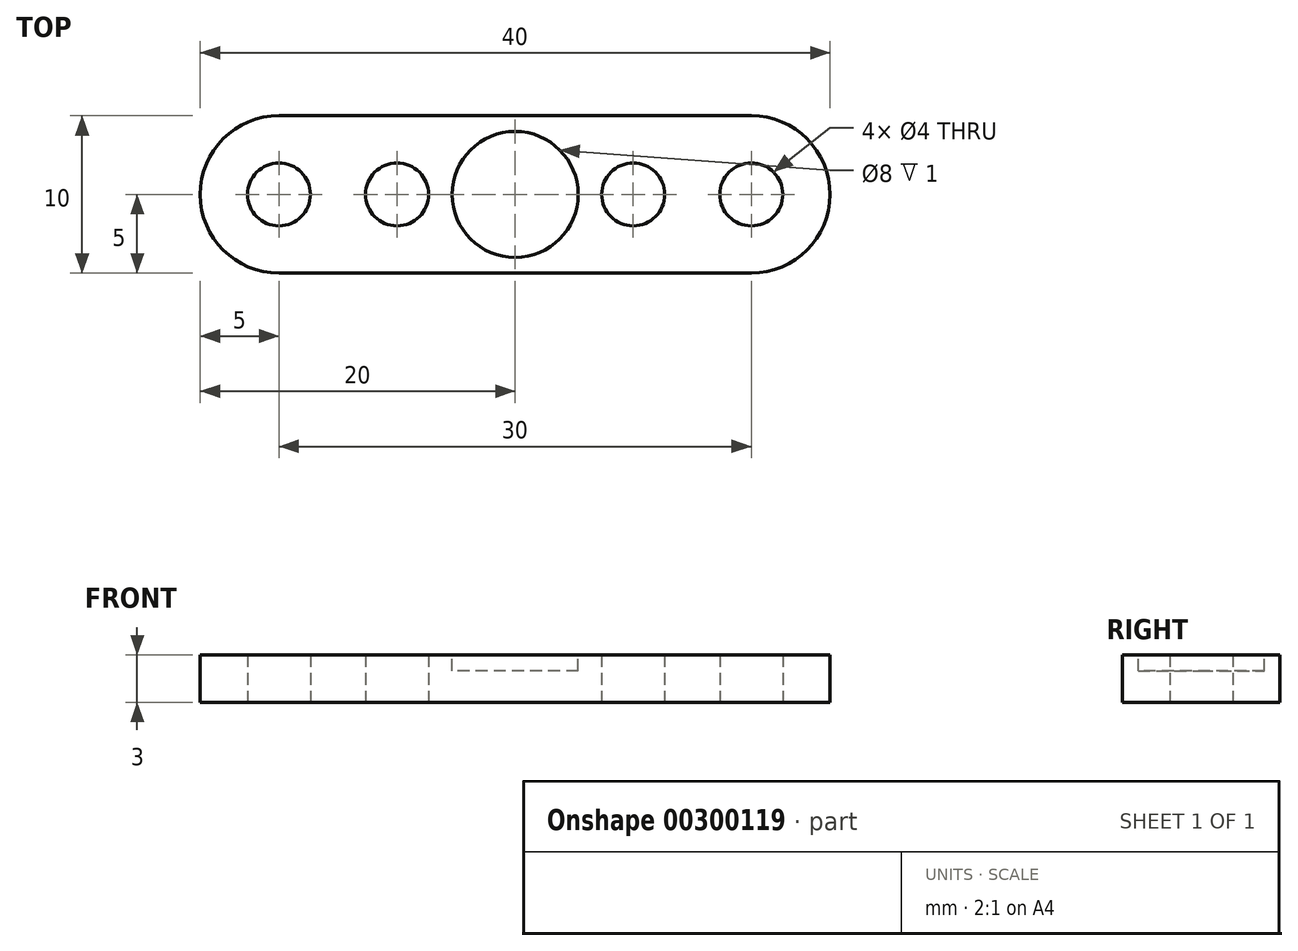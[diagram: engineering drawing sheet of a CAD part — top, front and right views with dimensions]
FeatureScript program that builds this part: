
annotation { "Feature Type Name" : "Feature", "Feature Type Description" : "" }
export const myFeature = defineFeature(function(context is Context, id is Id, definition is map)
    precondition{}
    {
        {
            var Q0;
            Q0=qCreatedBy(makeId("Top.planeOp"),FACE);
            var sketch = newSketch(context, id + "F0", { "sketchPlane" : qUnion([Q0])});
            skLineSegment(sketch, "E0.bottom", {"start": v(20, -5) * mm, "end": v(-20, -5) * mm});
            skLineSegment(sketch, "E0.top", {"start": v(20, 5) * mm, "end": v(-20, 5) * mm});
            skLineSegment(sketch, "E0.left", {"start": v(20, -5) * mm, "end": v(20, 5) * mm});
            skLineSegment(sketch, "E0.right", {"start": v(-20, -5) * mm, "end": v(-20, 5) * mm});
            skPoint(sketch, "E0.middle", {"position": v(0, 0) * mm});
            skSolve(sketch);
        }
        {
            var Q0;
            Q0 = qSketchRegion(id + "F0", true);
            extrude(context, id + "F1", {"entities" : qUnion([Q0]), "depth" : 3 * mm});
        }
        {
            var Q0;
            Q0=makeQuery(id+"F1.opExtrude","CAP_FACE",FACE,{"disambiguationData":[OSD([sQuery(id+"F0.wireOp",EDGE,"E0.bottom"),sQuery(id+"F0.wireOp",EDGE,"E0.top"),sQuery(id+"F0.wireOp",EDGE,"E0.left"),sQuery(id+"F0.wireOp",EDGE,"E0.right")])],"isStart":false});
            var sketch = newSketch(context, id + "F2", { "sketchPlane" : qUnion([Q0])});
            skCircle(sketch, "E1", {"center": v(0, 0) * mm, "radius": 4 * mm});
            skSolve(sketch);
        }
        {
            var Q0;
            Q0 = qSketchRegion(id + "F2", true);
            extrude(context, id + "F3", {"entities" : qUnion([Q0]), "operationType" : NewBodyOperationType.REMOVE, "oppositeDirection" : true, "depth" : 1 * mm});
        }
        {
            var Q0;
            Q0=qCreatedBy(makeId("Top.planeOp"),FACE);
            var sketch = newSketch(context, id + "F4", { "sketchPlane" : qUnion([Q0])});
            skCircle(sketch, "E2", {"center": v(-7.5, 0) * mm, "radius": 2 * mm});
            skCircle(sketch, "E3", {"center": v(7.5, 0) * mm, "radius": 2 * mm});
            skCircle(sketch, "E4", {"center": v(-15, 0) * mm, "radius": 2 * mm});
            skCircle(sketch, "E5", {"center": v(15, 0) * mm, "radius": 2 * mm});
            skSolve(sketch);
        }
        {
            var Q0;
            Q0 = qSketchRegion(id + "F4", true);
            extrude(context, id + "F5", {"entities" : qUnion([Q0]), "operationType" : NewBodyOperationType.REMOVE, "depth" : 25 * mm});
        }
        {
            var Q0;
            Q0=makeQuery(id+"F1.opExtrude","SWEPT_EDGE",EDGE,{"disambiguationData":[OSD([sQuery(id+"F0.wireOp",EDGE,"E0.bottom"),sQuery(id+"F0.wireOp",EDGE,"E0.right")])]});
            var Q1;
            Q1=makeQuery(id+"F1.opExtrude","SWEPT_EDGE",EDGE,{"disambiguationData":[OSD([sQuery(id+"F0.wireOp",EDGE,"E0.top"),sQuery(id+"F0.wireOp",EDGE,"E0.right")])]});
            var Q2;
            Q2=makeQuery(id+"F1.opExtrude","SWEPT_EDGE",EDGE,{"disambiguationData":[OSD([sQuery(id+"F0.wireOp",EDGE,"E0.bottom"),sQuery(id+"F0.wireOp",EDGE,"E0.left")])]});
            var Q3;
            Q3=makeQuery(id+"F1.opExtrude","SWEPT_EDGE",EDGE,{"disambiguationData":[OSD([sQuery(id+"F0.wireOp",EDGE,"E0.top"),sQuery(id+"F0.wireOp",EDGE,"E0.left")])]});
            fillet(context, id + "F6", {"entities" : qUnion([Q0, Q1, Q2, Q3]), "radius" : 5 * mm, "tangentPropagation" : true, "allowEdgeOverflow" : false});
        }
    });
